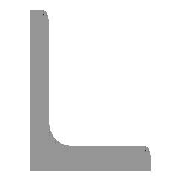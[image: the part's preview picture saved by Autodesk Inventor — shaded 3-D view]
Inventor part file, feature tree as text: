
AUTODESK INVENTOR PART (.ipt)
format: ipt  version: 2016 (Build 200138000, 138)  size: 119,808 bytes
history: native  units: mm (DEFAULTED — no unit token found)
features: other x4, sketch x2, extrude x1, plane x1
ambient origin geometry x8: Origin, YZ Plane, XZ Plane, XY Plane, X Axis, Y Axis, Z Axis, Center Point
bodies: Solid1 (feature_tree)
feature tree (8):
  parser-record x1  (decoder bookkeeping rows leaked as tree rows — omitted from the tree; the rows remain in map.json)
  other  "Driven Length"
  other  "Plano inicial"
  other  "Plano final"
  extrude  "Cuerpo"  Depth=38.1mm
  sketch  "Sketch3"  dims[d0=38.1mm d1=38.1mm]
  plane  "Work Plane3"
  sketch  "Sketch4"  dims[d2=4.7625mm d3=4.7625mm d4=1401.0mm d5=0.0mm d10=0.0mm d11=0.0mm d12=-0.0mm d13=1401.0mm d14=4.826mm d15=2.286mm d16=90.0deg d17=1401.0mm]
